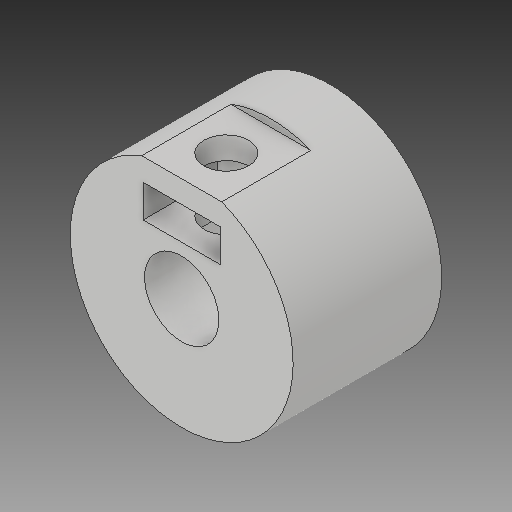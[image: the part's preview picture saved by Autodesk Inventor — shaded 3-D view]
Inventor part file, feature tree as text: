
AUTODESK INVENTOR PART (.ipt)
format: ipt  version: 2019 (Build 230136000, 136)  size: 142,336 bytes
history: native  units: mm
features: extrude x4, sketch x4, plane x1
ambient origin geometry x8: Origin, YZ Plane, XZ Plane, XY Plane, X Axis, Y Axis, Z Axis, Center Point
bodies: Solid1 (feature_tree)
feature tree (9):
  extrude  "Extrusion1"  Depth=5.0mm
  plane  "Work Plane1"
  extrude  "Extrusion2"  Depth=10.0mm
  extrude  "Extrusion3"  Depth=2.2mm
  extrude  "Extrusion4"  Depth=10.0mm TaperAngle=0.0deg
  sketch  "Sketch1"  dims[d0=15.0mm d1=5.0mm]
  sketch  "Sketch2"  dims[d2=10.0mm d3=0.0mm d4=5.0mm]
  sketch  "Sketch4"  dims[d5=5.5mm d6=2.2mm]
  sketch  "Sketch5"  dims[d7=5.2mm d8=5.0mm d9=0.0mm d12=3.0mm d13=7.0mm d14=8.0mm d15=0.0mm d16=6.0mm d17=10.0mm d18=0.5mm d19=8.0mm d20=0.0mm]
